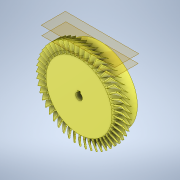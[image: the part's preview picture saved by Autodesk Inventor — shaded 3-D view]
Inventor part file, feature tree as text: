
AUTODESK INVENTOR PART (.ipt)
format: ipt  version: 2021.2 (Build 252289000, 289)  size: 2,782,720 bytes
history: native  units: in
note: dims shown in document units (in); Inventor stores cm internally (conversion verified against a paired STEP export)
features: sketch x5, extrude x4, plane x2, loft x1, pattern_circular x1, other x1
ambient origin geometry x8: Origin, YZ Plane, XZ Plane, XY Plane, X Axis, Y Axis, Z Axis, Center Point
bodies: Solid1 (feature_tree)
feature tree (14):
  extrude  "Extrusion1"  Depth=0.9688in
  plane  "Work Plane1"
  extrude  "Extrusion2"  Depth=0.0312in
  plane  "Work Plane2"
  loft  "Loft3"
  pattern_circular  "Circular Pattern6"  Count=48 Angle=360.0deg
  extrude  "Extrusion3"  Depth=0.315in
  extrude  "Extrusion4"  Depth=0.125in
  sketch  "Sketch1"  dims[d0=3.0in d1=0.9688in d2=0.0777in]
  sketch  "Sketch2"  dims[d3=1.6in d4=0.0312in]
  sketch  "Sketch4"  dims[d5=0.5in d6=0.0in d13=2.0in]
  other  "Edges3"
  sketch  "Sketch5"  dims[d28=0.0in d29=90.0deg]
  sketch  "Sketch6"  dims[d30=0.0in d31=90.0deg d35=18.8976in d36=360.0deg d38=0.315in d39=0.125in d40=0.125in d41=0.0in d42=0.0in d43=3.9375in d44=0.0in d45=0.0in]
